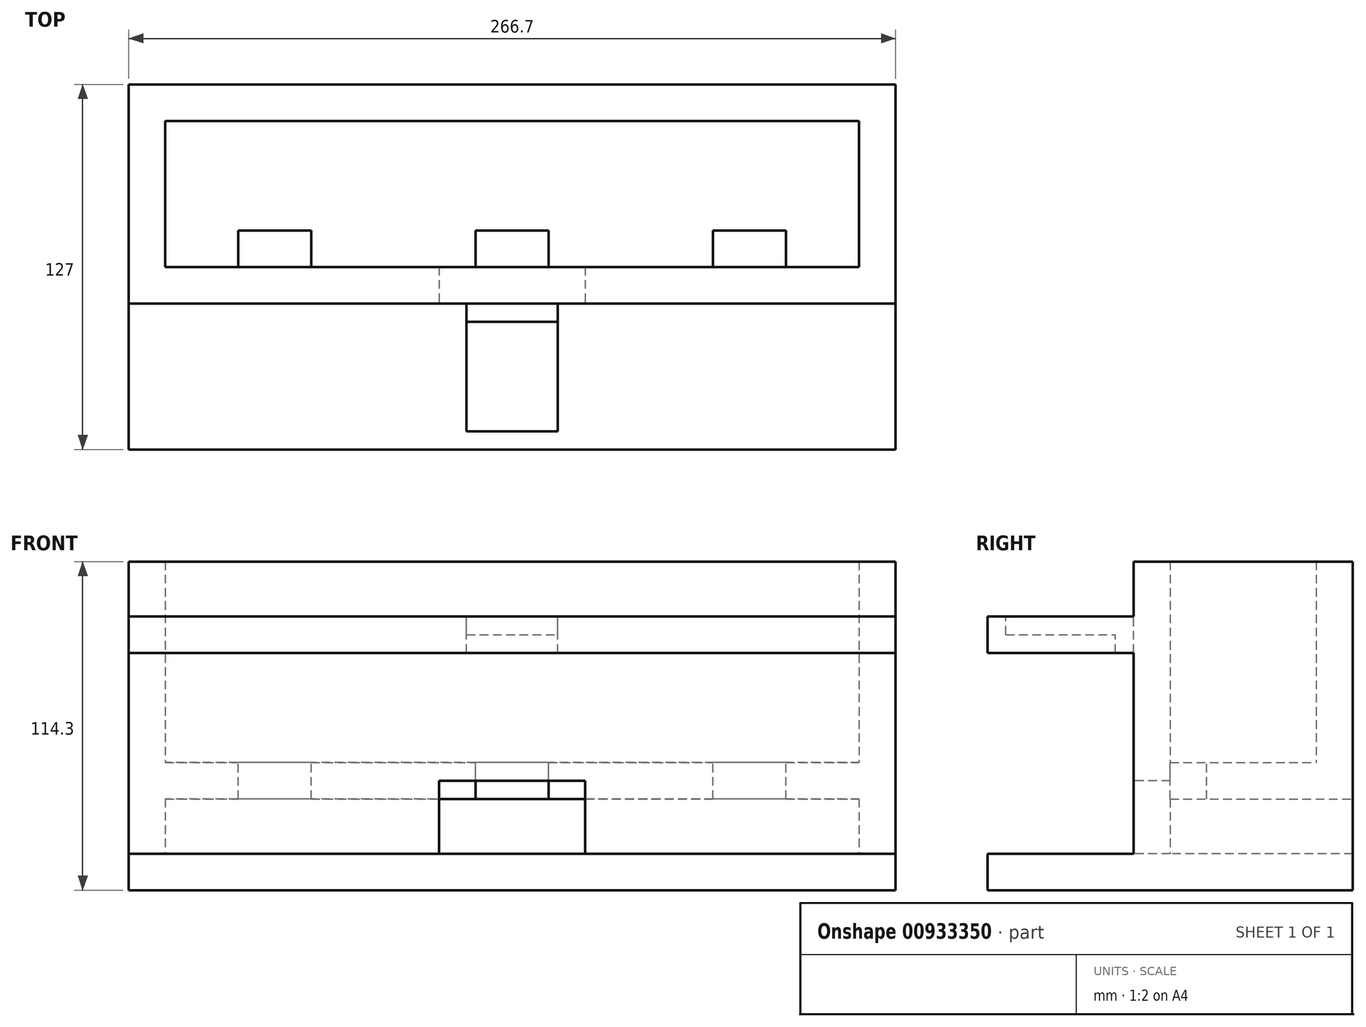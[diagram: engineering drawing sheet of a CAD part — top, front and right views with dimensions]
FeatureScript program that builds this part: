
annotation { "Feature Type Name" : "Feature", "Feature Type Description" : "" }
export const myFeature = defineFeature(function(context is Context, id is Id, definition is map)
    precondition{}
    {
        {
            var Q0;
            Q0=qCreatedBy(makeId("Top.planeOp"),FACE);
            var sketch = newSketch(context, id + "F0", { "sketchPlane" : qUnion([Q0])});
            skLineSegment(sketch, "E0.bottom", {"start": v(0, 0) * mm, "end": v(266.7, 0) * mm});
            skLineSegment(sketch, "E0.top", {"start": v(0, 127) * mm, "end": v(266.7, 127) * mm});
            skLineSegment(sketch, "E0.left", {"start": v(0, 0) * mm, "end": v(0, 127) * mm});
            skLineSegment(sketch, "E0.right", {"start": v(266.7, 0) * mm, "end": v(266.7, 127) * mm});
            skSolve(sketch);
        }
        {
            var Q0;
            Q0=makeQuery(id+"F0.imprint","IMPRINT",FACE,{"disambiguationData":[TD([[makeQuery(id+"F0.imprint","IMPRINT",EDGE,{"derivedFrom":sQuery(id+"F0.wireOp",EDGE,"E0.bottom")}),1.0]])]});
            extrude(context, id + "F1", {"entities" : qUnion([Q0]), "depth" : 12.7 * mm, "offsetDistance" : 25.4 * mm});
        }
        {
            var Q0;
            Q0=makeQuery(id+"F1.opExtrude","CAP_FACE",FACE,{"disambiguationData":[OSD([sQuery(id+"F0.wireOp",EDGE,"E0.bottom"),sQuery(id+"F0.wireOp",EDGE,"E0.top"),sQuery(id+"F0.wireOp",EDGE,"E0.left"),sQuery(id+"F0.wireOp",EDGE,"E0.right")])],"isStart":false});
            var sketch = newSketch(context, id + "F2", { "sketchPlane" : qUnion([Q0])});
            skLineSegment(sketch, "E1.bottom", {"start": v(0, 50.8) * mm, "end": v(266.7, 50.8) * mm});
            skLineSegment(sketch, "E1.top", {"start": v(12.7, 63.5) * mm, "end": v(254, 63.5) * mm});
            skLineSegment(sketch, "E1.left", {"start": v(0, 50.8) * mm, "end": v(0, 63.5) * mm});
            skLineSegment(sketch, "E1.right", {"start": v(266.7, 50.8) * mm, "end": v(266.7, 63.5) * mm});
            skLineSegment(sketch, "E2.bottom", {"start": v(0, 127) * mm, "end": v(266.7, 127) * mm});
            skLineSegment(sketch, "E2.top", {"start": v(12.7, 114.3) * mm, "end": v(254, 114.3) * mm});
            skLineSegment(sketch, "E2.left", {"start": v(0, 127) * mm, "end": v(0, 114.3) * mm});
            skLineSegment(sketch, "E2.right", {"start": v(266.7, 127) * mm, "end": v(266.7, 114.3) * mm});
            skLineSegment(sketch, "E3.left", {"start": v(0, 114.3) * mm, "end": v(0, 63.5) * mm});
            skLineSegment(sketch, "E3.right", {"start": v(12.7, 114.3) * mm, "end": v(12.7, 63.5) * mm});
            skLineSegment(sketch, "E4.left", {"start": v(266.7, 114.3) * mm, "end": v(266.7, 63.5) * mm});
            skLineSegment(sketch, "E4.right", {"start": v(254, 114.3) * mm, "end": v(254, 63.5) * mm});
            skSolve(sketch);
        }
        {
            var Q0;
            Q0 = qSketchRegion(id + "F2", true);
            extrude(context, id + "F3", {"entities" : qUnion([Q0]), "operationType" : NewBodyOperationType.ADD, "depth" : 101.6 * mm, "offsetDistance" : 25.4 * mm});
        }
        {
            var Q0;
            Q0=makeQuery(id+"F3.opExtrude","SWEPT_FACE",FACE,{"disambiguationData":[OSD([sQuery(id+"F2.wireOp",EDGE,"E1.bottom")])]});
            var sketch = newSketch(context, id + "F4", { "sketchPlane" : qUnion([Q0])});
            skLineSegment(sketch, "E5.bottom", {"start": v(0, 82.55) * mm, "end": v(266.7, 82.55) * mm});
            skLineSegment(sketch, "E5.top", {"start": v(0, 95.25) * mm, "end": v(266.7, 95.25) * mm});
            skLineSegment(sketch, "E5.left", {"start": v(0, 82.55) * mm, "end": v(0, 95.25) * mm});
            skLineSegment(sketch, "E5.right", {"start": v(266.7, 82.55) * mm, "end": v(266.7, 95.25) * mm});
            skSolve(sketch);
        }
        {
            var Q0;
            Q0 = qSketchRegion(id + "F4", true);
            var Q1;
            Q1=makeQuery(id+"F1.opExtrude","SWEPT_FACE",FACE,{"disambiguationData":[OSD([sQuery(id+"F0.wireOp",EDGE,"E0.bottom")])]});
            extrude(context, id + "F5", {"entities" : qUnion([Q0]), "operationType" : NewBodyOperationType.ADD, "endBound" : BoundingType.UP_TO_SURFACE, "depth" : 25.4 * mm, "endBoundEntityFace" : qUnion([Q1]), "offsetDistance" : 25.4 * mm});
        }
        {
            var Q0;
            Q0=makeQuery(id+"F3.boolean.opBoolean","MERGE",FACE,{"derivedFrom":[makeQuery(id+"F1.opExtrude","SWEPT_FACE",FACE,{"disambiguationData":[OSD([sQuery(id+"F0.wireOp",EDGE,"E0.top")])]}),makeQuery(id+"F3.opExtrude","SWEPT_FACE",FACE,{"disambiguationData":[OSD([sQuery(id+"F2.wireOp",EDGE,"E2.bottom")])]})]});
            var sketch = newSketch(context, id + "F6", { "sketchPlane" : qUnion([Q0])});
            skLineSegment(sketch, "E6.bottom", {"start": v(-254, 31.75) * mm, "end": v(-12.7, 31.75) * mm});
            skLineSegment(sketch, "E6.top", {"start": v(-254, 12.7) * mm, "end": v(-12.7, 12.7) * mm});
            skLineSegment(sketch, "E6.left", {"start": v(-254, 31.75) * mm, "end": v(-254, 12.7) * mm});
            skLineSegment(sketch, "E6.right", {"start": v(-12.7, 31.75) * mm, "end": v(-12.7, 12.7) * mm});
            skSolve(sketch);
        }
        {
            var Q0;
            Q0 = qSketchRegion(id + "F6", true);
            var Q1;
            Q1=makeQuery(id+"F3.opExtrude","SWEPT_FACE",FACE,{"disambiguationData":[OSD([sQuery(id+"F2.wireOp",EDGE,"E1.top")])]});
            extrude(context, id + "F7", {"entities" : qUnion([Q0]), "operationType" : NewBodyOperationType.REMOVE, "endBound" : BoundingType.UP_TO_SURFACE, "oppositeDirection" : true, "depth" : 25.4 * mm, "endBoundEntityFace" : qUnion([Q1]), "offsetDistance" : 25.4 * mm});
        }
        {
            var Q0;
            Q0=makeQuery(id+"F5.boolean.opBoolean","SPLIT",FACE,{"disambiguationData":[TD([makeQuery(id+"F5.opExtrude","SWEPT_FACE",FACE,{"disambiguationData":[OSD([sQuery(id+"F4.wireOp",EDGE,"E5.bottom")])]})])],"derivedFrom":makeQuery(id+"F3.opExtrude","SWEPT_FACE",FACE,{"disambiguationData":[OSD([sQuery(id+"F2.wireOp",EDGE,"E1.bottom")])]})});
            var sketch = newSketch(context, id + "F8", { "sketchPlane" : qUnion([Q0])});
            skLineSegment(sketch, "E7.bottom", {"start": v(107.95, 12.7) * mm, "end": v(158.75, 12.7) * mm});
            skLineSegment(sketch, "E7.top", {"start": v(107.95, 38.1) * mm, "end": v(158.75, 38.1) * mm});
            skLineSegment(sketch, "E7.left", {"start": v(107.95, 12.7) * mm, "end": v(107.95, 38.1) * mm});
            skLineSegment(sketch, "E7.right", {"start": v(158.75, 12.7) * mm, "end": v(158.75, 38.1) * mm});
            skLineSegment(sketch, "E8", {"start": v(133.35, 12.7) * mm, "end": v(133.35, 82.55) * mm, "construction": true});
            skSolve(sketch);
        }
        {
            var Q0;
            Q0 = qSketchRegion(id + "F8", true);
            var Q1;
            Q1=makeQuery(id+"F3.opExtrude","SWEPT_FACE",FACE,{"disambiguationData":[OSD([sQuery(id+"F2.wireOp",EDGE,"E2.top")])]});
            extrude(context, id + "F9", {"entities" : qUnion([Q0]), "operationType" : NewBodyOperationType.REMOVE, "endBound" : BoundingType.UP_TO_SURFACE, "oppositeDirection" : true, "depth" : 25.4 * mm, "endBoundEntityFace" : qUnion([Q1]), "offsetDistance" : 25.4 * mm});
        }
        {
            var Q0;
            Q0=makeQuery(id+"F5.opExtrude","SWEPT_FACE",FACE,{"disambiguationData":[OSD([sQuery(id+"F4.wireOp",EDGE,"E5.top")])]});
            var sketch = newSketch(context, id + "F10", { "sketchPlane" : qUnion([Q0])});
            skLineSegment(sketch, "E9.bottom", {"start": v(117.48, 6.35) * mm, "end": v(149.23, 6.35) * mm});
            skLineSegment(sketch, "E9.top", {"start": v(117.48, 50.8) * mm, "end": v(149.23, 50.8) * mm});
            skLineSegment(sketch, "E9.left", {"start": v(117.48, 6.35) * mm, "end": v(117.48, 50.8) * mm});
            skLineSegment(sketch, "E9.right", {"start": v(149.23, 6.35) * mm, "end": v(149.23, 50.8) * mm});
            skSolve(sketch);
        }
        {
            var Q0;
            Q0 = qSketchRegion(id + "F10", true);
            extrude(context, id + "F11", {"entities" : qUnion([Q0]), "operationType" : NewBodyOperationType.REMOVE, "oppositeDirection" : true, "depth" : 6.35 * mm, "offsetDistance" : 25.4 * mm});
        }
        {
            var Q0;
            Q0=makeQuery(id+"F3.boolean.opBoolean","MERGE",FACE,{"derivedFrom":[makeQuery(id+"F1.opExtrude","SWEPT_FACE",FACE,{"disambiguationData":[OSD([sQuery(id+"F0.wireOp",EDGE,"E0.top")])]}),makeQuery(id+"F3.opExtrude","SWEPT_FACE",FACE,{"disambiguationData":[OSD([sQuery(id+"F2.wireOp",EDGE,"E2.bottom")])]})]});
            var sketch = newSketch(context, id + "F12", { "sketchPlane" : qUnion([Q0])});
            skLineSegment(sketch, "E10.bottom", {"start": v(-254, 31.75) * mm, "end": v(-12.7, 31.75) * mm});
            skLineSegment(sketch, "E10.top", {"start": v(-254, 44.45) * mm, "end": v(-12.7, 44.45) * mm});
            skLineSegment(sketch, "E10.left", {"start": v(-254, 31.75) * mm, "end": v(-254, 44.45) * mm});
            skLineSegment(sketch, "E10.right", {"start": v(-12.7, 31.75) * mm, "end": v(-12.7, 44.45) * mm});
            skSolve(sketch);
        }
        {
            var Q0;
            Q0 = qSketchRegion(id + "F12", true);
            var Q1;
            Q1=makeQuery(id+"F3.opExtrude","SWEPT_FACE",FACE,{"disambiguationData":[OSD([sQuery(id+"F2.wireOp",EDGE,"E1.top")])]});
            extrude(context, id + "F13", {"entities" : qUnion([Q0]), "operationType" : NewBodyOperationType.ADD, "endBound" : BoundingType.UP_TO_SURFACE, "oppositeDirection" : true, "depth" : 25.4 * mm, "endBoundEntityFace" : qUnion([Q1]), "offsetDistance" : 25.4 * mm});
        }
        {
            var Q0;
            Q0=makeQuery(id+"F11.boolean.opBoolean","COPY",FACE,{"derivedFrom":makeQuery(id+"F11.opExtrude","CAP_FACE",FACE,{"disambiguationData":[OSD([sQuery(id+"F10.wireOp",EDGE,"E9.bottom"),sQuery(id+"F10.wireOp",EDGE,"E9.top"),sQuery(id+"F10.wireOp",EDGE,"E9.left"),sQuery(id+"F10.wireOp",EDGE,"E9.right")])],"isStart":false})});
            var sketch = newSketch(context, id + "F14", { "sketchPlane" : qUnion([Q0])});
            skLineSegment(sketch, "E11.bottom", {"start": v(117.48, 50.8) * mm, "end": v(149.23, 50.8) * mm});
            skLineSegment(sketch, "E11.top", {"start": v(117.48, 44.45) * mm, "end": v(149.23, 44.45) * mm});
            skLineSegment(sketch, "E11.left", {"start": v(117.48, 50.8) * mm, "end": v(117.48, 44.45) * mm});
            skLineSegment(sketch, "E11.right", {"start": v(149.23, 50.8) * mm, "end": v(149.23, 44.45) * mm});
            skSolve(sketch);
        }
        {
            var Q0;
            Q0 = qSketchRegion(id + "F14", true);
            extrude(context, id + "F15", {"entities" : qUnion([Q0]), "operationType" : NewBodyOperationType.REMOVE, "endBound" : BoundingType.UP_TO_NEXT, "oppositeDirection" : true, "depth" : 25.4 * mm, "offsetDistance" : 25.4 * mm});
        }
        {
            var Q0;
            Q0=makeQuery(id+"F13.opExtrude","SWEPT_FACE",FACE,{"disambiguationData":[OSD([sQuery(id+"F12.wireOp",EDGE,"E10.top")])]});
            var sketch = newSketch(context, id + "F16", { "sketchPlane" : qUnion([Q0])});
            skLineSegment(sketch, "E12.bottom", {"start": v(228.6, 63.5) * mm, "end": v(203.2, 63.5) * mm});
            skLineSegment(sketch, "E12.top", {"start": v(228.6, 76.2) * mm, "end": v(203.2, 76.2) * mm});
            skLineSegment(sketch, "E12.left", {"start": v(228.6, 63.5) * mm, "end": v(228.6, 76.2) * mm});
            skLineSegment(sketch, "E12.right", {"start": v(203.2, 63.5) * mm, "end": v(203.2, 76.2) * mm});
            skLineSegment(sketch, "E13.bottom", {"start": v(63.5, 63.5) * mm, "end": v(38.1, 63.5) * mm});
            skLineSegment(sketch, "E13.top", {"start": v(63.5, 76.2) * mm, "end": v(38.1, 76.2) * mm});
            skLineSegment(sketch, "E13.left", {"start": v(63.5, 63.5) * mm, "end": v(63.5, 76.2) * mm});
            skLineSegment(sketch, "E13.right", {"start": v(38.1, 63.5) * mm, "end": v(38.1, 76.2) * mm});
            skLineSegment(sketch, "E14.bottom", {"start": v(146.05, 63.5) * mm, "end": v(120.65, 63.5) * mm});
            skLineSegment(sketch, "E14.top", {"start": v(146.05, 76.2) * mm, "end": v(120.65, 76.2) * mm});
            skLineSegment(sketch, "E14.left", {"start": v(146.05, 63.5) * mm, "end": v(146.05, 76.2) * mm});
            skLineSegment(sketch, "E14.right", {"start": v(120.65, 63.5) * mm, "end": v(120.65, 76.2) * mm});
            skSolve(sketch);
        }
        {
            var Q0;
            Q0 = qSketchRegion(id + "F16", true);
            extrude(context, id + "F17", {"entities" : qUnion([Q0]), "operationType" : NewBodyOperationType.REMOVE, "endBound" : BoundingType.UP_TO_NEXT, "oppositeDirection" : true, "depth" : 25.4 * mm, "offsetDistance" : 25.4 * mm});
        }
    });
